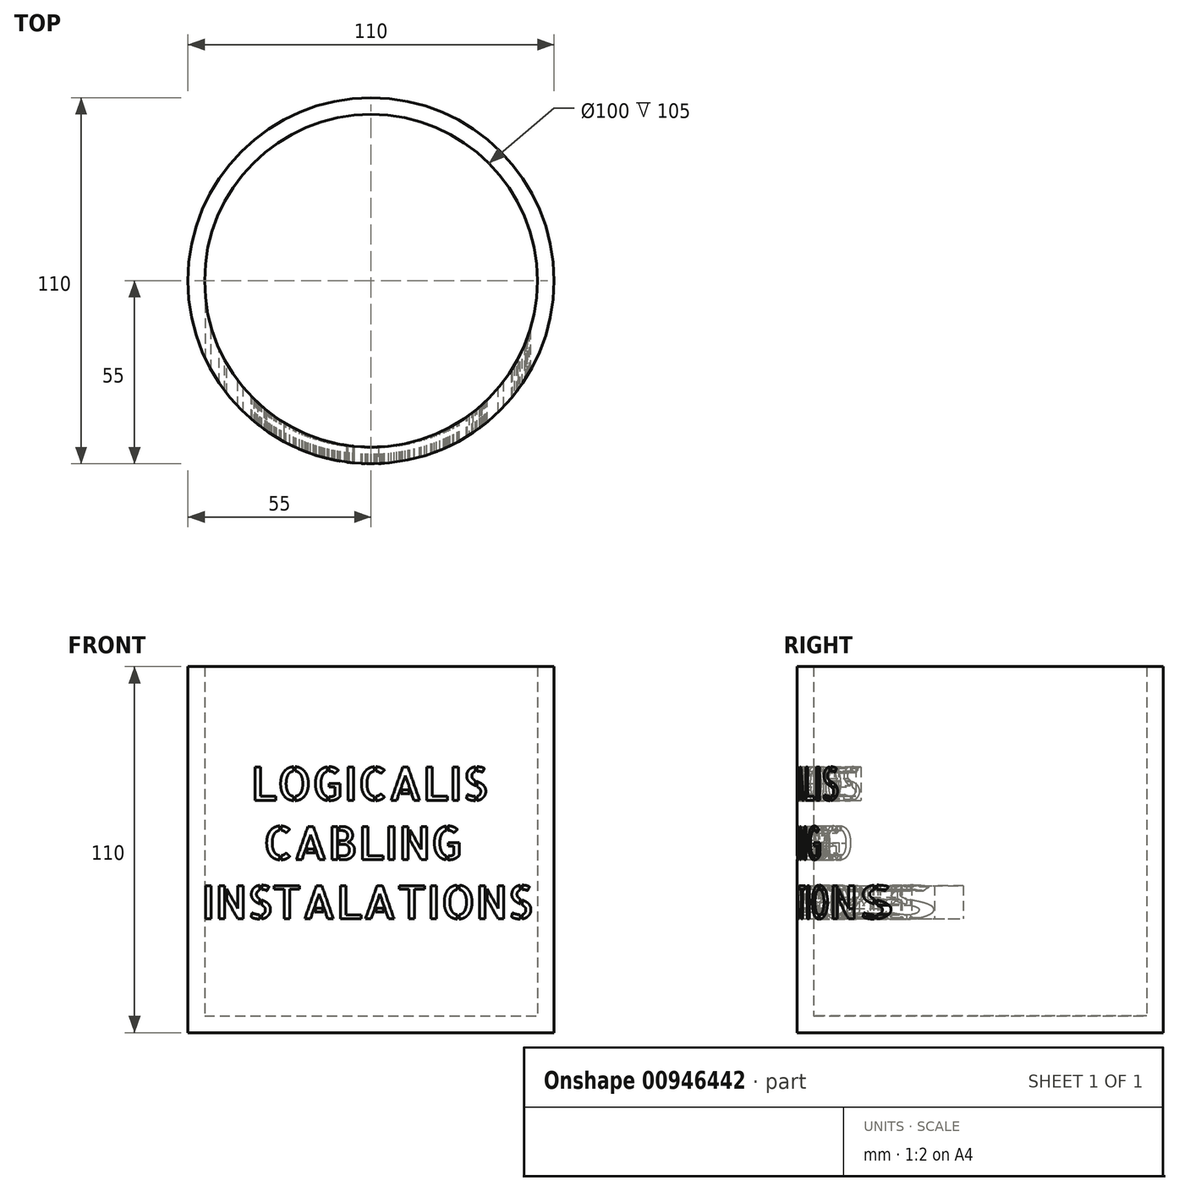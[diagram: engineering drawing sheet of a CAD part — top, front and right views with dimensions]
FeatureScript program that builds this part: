
annotation { "Feature Type Name" : "Feature", "Feature Type Description" : "" }
export const myFeature = defineFeature(function(context is Context, id is Id, definition is map)
    precondition{}
    {
        {
            var Q0;
            Q0=qCreatedBy(makeId("Front.planeOp"),FACE);
            var sketch = newSketch(context, id + "F0", { "sketchPlane" : qUnion([Q0])});
            skLineSegment(sketch, "E0.top", {"start": v(-55, 110) * mm, "end": v(-50, 110) * mm});
            skLineSegment(sketch, "E0.left", {"start": v(-55, 0) * mm, "end": v(-55, 110) * mm});
            skLineSegment(sketch, "E0.right", {"start": v(-50, 5) * mm, "end": v(-50, 110) * mm});
            skLineSegment(sketch, "E1.top", {"start": v(-50, 5) * mm, "end": v(0, 5) * mm});
            skLineSegment(sketch, "E1.right", {"start": v(0, 0) * mm, "end": v(0, 5) * mm});
            skLineSegment(sketch, "E2", {"start": v(-55, 0) * mm, "end": v(0, 0) * mm});
            skSolve(sketch);
        }
        {
            var Q0;
            Q0=makeQuery(id+"F0.imprint","IMPRINT",FACE,{"disambiguationData":[TD([[makeQuery(id+"F0.imprint","IMPRINT",EDGE,{"derivedFrom":sQuery(id+"F0.wireOp",EDGE,"E0.top")}),-1.0]])]});
            var Q1;
            Q1=sQuery(id+"F0.wireOp",EDGE,"E1.right");
            revolve(context, id + "F1", {"surfaceOperationType" : NewSurfaceOperationType.NEW, "entities" : qUnion([Q0]), "axis" : qUnion([Q1]), "revolveType" : RevolveType.FULL});
        }
        {
            var Q0;
            Q0=qCreatedBy(makeId("Front.planeOp"),FACE);
            var sketch = newSketch(context, id + "F2", { "sketchPlane" : qUnion([Q0])});
            skText(sketch, "E3", { "text": "    LOGICALIS\n     CABLING\nINSTALATIONS", "fontName": "AllertaStencil-Regular.ttf"});
            const initialGuessF2  = {"E3": [-0.05102, 0.06978, 1, 0, 0.01001]};
            skSetInitialGuess(sketch, initialGuessF2);
            skSolve(sketch);
        }
        {
            var Q0;
            Q0 = qSketchRegion(id + "F2", true);
            var Q1;
            Q1 = qConstructionFilter(qBodyType(qCreatedBy(id + "F2" ,EDGE), BodyType.WIRE), ConstructionObject.NO);
            extrude(context, id + "F3", {"entities" : qUnion([Q0]), "operationType" : NewBodyOperationType.REMOVE, "surfaceEntities" : qUnion([Q1]), "endBound" : BoundingType.THROUGH_ALL, "depth" : 91 * mm, "offsetDistance" : 25 * mm});
        }
    });
